# Revit family: Комплект мебели «Пикник2» Арт 9610
name_source: partatom
category: Антураж
revit_build: Autodesk Revit 2018 (Build: 20180423_1000(x64)
units: mm (PartAtom-declared; Revit-internal decimal feet)

## family parameters
Всегда вертикально = Да
Источник визуального образа = Геометрия семейства
На основе рабочей плоскости = Нет
Общий = Нет
При загрузке вырезать с полостями = Нет
Точка расчета площади = Нет

## types (3) — shared parameters
URL = https://hobbyka.ru
Артикул товара = Арт. 9610
Высота = 790 мм
Группа модели = Садовые столы
Изготовитель = ООО «Хоббика»
Изображение типоразмера = Комплект мебели «Пикник2» Арт 9610.jpg
Материал изделия = Сталь, дерево
Цвет каркаса = Сталь
Цвет отделки = Дерево
Ширина = 1590 мм

## per-type parameters (varying)
| type | Длина | Описание | Стандарт | Стандарт плюс | Шахматная доска стандарт |
| Версия "Стандарт" | 1800 мм | Комплект мебели «Пикник2». Стандарт | Да | Нет | Нет |
| Версия "Стандарт плюс" | 2400 мм | Комплект мебели «Пикник2. Стандарт плюс» | Нет | Да | Нет |
| Версия "Шахматная доска стандарт" | 1800 мм | Комплект мебели «Пикник2. Стандарт с шахматной доской | Нет | Нет | Да |
